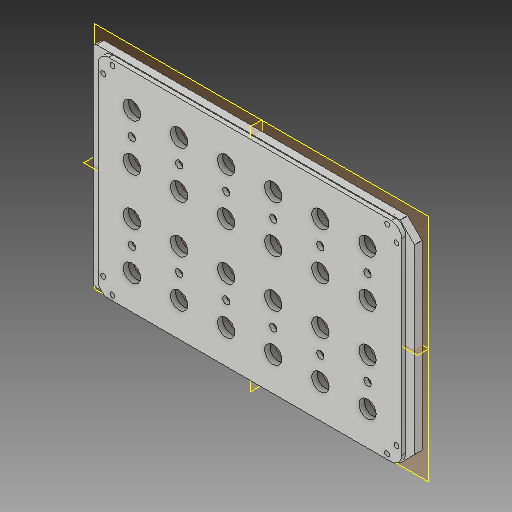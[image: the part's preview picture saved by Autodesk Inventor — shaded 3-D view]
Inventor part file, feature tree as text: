
AUTODESK INVENTOR PART (.ipt)
format: ipt  version: 2019.4 (Build 234330000, 330)  size: 410,624 bytes
history: native  units: mm
features: reference x41, other x20, sketch x6, plane x4, extrude x4, projected_geometry x3, hole x2, pattern_linear x1
ambient origin geometry x8: Origin, YZ Plane, XZ Plane, XY Plane, X Axis, Y Axis, Z Axis, Center Point
bodies: Volumenkörper1 (feature_tree)
feature tree (81):
  plane  "Arbeitsebene1"
  extrude  "Extrusion1"  Depth=2.0mm TaperAngle=0.0deg
  extrude  "Extrusion2"  Depth=2.0mm TaperAngle=0.0deg
  extrude  "Extrusion3"  Depth=20.0mm
  pattern_linear  "Rechteckige Anordnung1"  Count1=6 Spacing1=18.0mm
  plane  "Arbeitsebene2"
  plane  "Arbeitsebene3"
  sketch  "Skizze5"  dims[d21=0.5mm d22=0.5mm]
  plane  "Arbeitsebene4"
  extrude  "Extrusion4"  Depth=0.5mm
  hole  "Hole2"  [1 undecoded]
  hole  "Hole3"  [1 undecoded]
  sketch  "Skizze1"  dims[d0=2.5mm d1=0.0mm d2=2.0mm d3=0.0mm]
  reference  "Referenz1"
  reference  "Referenz2"
  reference  "Referenz3"
  reference  "Referenz4"
  reference  "Referenz5"
  reference  "Referenz6"
  reference  "Referenz7"
  reference  "Referenz8"
  reference  "Referenz9"
  reference  "Referenz10"
  reference  "Referenz11"
  reference  "Referenz12"
  reference  "Referenz13"
  reference  "Referenz14"
  reference  "Referenz15"
  reference  "Referenz16"
  reference  "Referenz17"
  reference  "Referenz18"
  reference  "Referenz19"
  reference  "Referenz20"
  reference  "Referenz21"
  reference  "Referenz22"
  reference  "Referenz23"
  reference  "Referenz24"
  reference  "Referenz25"
  reference  "Referenz26"
  reference  "Referenz27"
  reference  "Referenz28"
  reference  "Referenz29"
  reference  "Referenz30"
  reference  "Referenz31"
  reference  "Referenz32"
  reference  "Referenz33"
  reference  "Referenz34"
  reference  "Referenz35"
  reference  "Referenz36"
  reference  "Referenz37"
  reference  "Referenz38"
  sketch  "Skizze2"  dims[d4=6.6mm d5=2.0mm d6=0.0mm]
  projected_geometry  "Projizierte Kontur1"
  sketch  "Skizze3"  dims[d7=6.6mm d15=20.0mm d17=36.0mm d18=60.0mm d20=18.0mm]
  reference  "Referenz39"
  reference  "Referenz40"
  reference  "Referenz41"
  sketch  "Sketch7"  dims[d23=2.0mm d24=0.0mm]
  projected_geometry  "Projected Loop3"
  sketch  "Sketch8"  dims[d27=1.9mm d28=6.0mm d29=4.0mm d30=2.0mm d31=90.0deg d32=12.0mm d33=20.594885mm d34=2.8mm d35=6.0mm d36=6.0mm d37=3.0mm d38=90.0deg d39=12.0mm d40=20.594885mm]
  projected_geometry  "Projected Loop4"
  other  "Full_HITscope_v0.iam"
  other  "05_Omniscope_base_v1:1"
  other  "Assembly_Omniscope_v1:12"
  other  "01_Camera_Module_left_v0:1"
  other  "Assembly_Omniscope_v1:10"
  other  "Assembly_Omniscope_v1:8"
  other  "Assembly_Omniscope_v1:6"
  other  "Assembly_Omniscope_v1:4"
  other  "Assembly_Omniscope_v1:2"
  other  "Assembly_Omniscope_v1:1"
  other  "Assembly_Omniscope_v1:3"
  other  "Assembly_Omniscope_v1:5"
  other  "Assembly_Omniscope_v1:7"
  other  "Assembly_Omniscope_v1:9"
  other  "Assembly_Omniscope_v1:11"
  other  "00_ESP32_Board:1"
  other  "00_ESP32_Board:2"
  other  "03_Camera_Clip:1"
  other  "00_MTP_96-welplate:1"
  other  "<userpath>\Documents\Inventor\HITscope\Full_HITscope_v0.iam"
note: 2 required parameter values undecoded (feature->parameter linkage not recoverable at this tier; creation-order binding heuristic only, values carry confidence <= 0.55)
